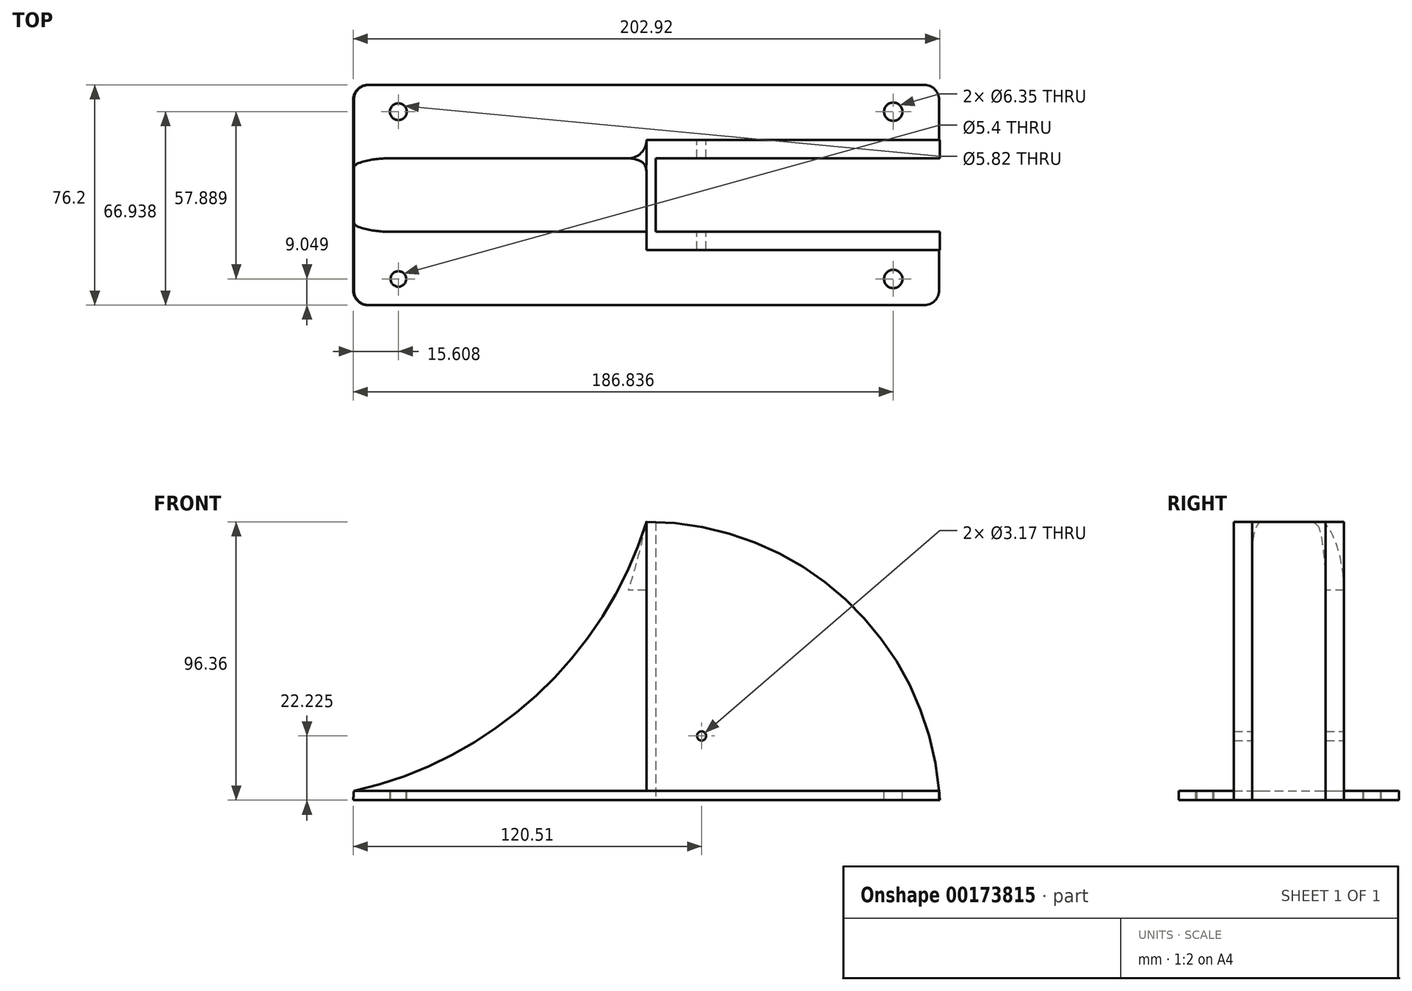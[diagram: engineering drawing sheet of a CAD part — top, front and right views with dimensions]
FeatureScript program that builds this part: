
annotation { "Feature Type Name" : "Feature", "Feature Type Description" : "" }
export const myFeature = defineFeature(function(context is Context, id is Id, definition is map)
    precondition{}
    {
        {
            var Q0;
            Q0=qCreatedBy(makeId("Front.planeOp"),FACE);
            var sketch = newSketch(context, id + "F0", { "sketchPlane" : qUnion([Q0])});
            skLineSegment(sketch, "E0", {"start": v(-101.6, 0) * mm, "end": v(101.6, 0) * mm});
            skArc(sketch, "E1", {"start": v(101.46, 0) * mm, "mid": v(69.96, 68.43) * mm, "end": v(0, 96.36) * mm});
            skLineSegment(sketch, "E2.bottom", {"start": v(-101.6, 0) * mm, "end": v(101.25, 0) * mm});
            skLineSegment(sketch, "E2.top", {"start": v(-101.6, 3.18) * mm, "end": v(101.25, 3.18) * mm});
            skLineSegment(sketch, "E2.left", {"start": v(-101.6, 0) * mm, "end": v(-101.6, 3.18) * mm});
            skLineSegment(sketch, "E2.right", {"start": v(101.25, 0) * mm, "end": v(101.25, 3.18) * mm});
            skLineSegment(sketch, "E3", {"start": v(0, 96.36) * mm, "end": v(0, 3.18) * mm});
            skArc(sketch, "E4", {"start": v(-101.25, 3.18) * mm, "mid": v(-38.14, 36.2) * mm, "end": v(0, 96.36) * mm});
            skArc(sketch, "E5", {"start": v(-101.25, 3.18) * mm, "mid": v(-101.37, 1.59) * mm, "end": v(-101.46, 0) * mm});
            skCircle(sketch, "E6", {"center": v(19.05, 22.23) * mm, "radius": 1.59 * mm});
            skSolve(sketch);
        }
        {
            var Q0;
            {var subQ5=sQuery(id+"F0.wireOp",EDGE,"E2.right");Q0=makeQuery(id+"F0.imprint","IMPRINT",FACE,{"disambiguationData":[TD([[makeQuery(id+"F0.imprint","IMPRINT",EDGE,{"derivedFrom":subQ5}),1.0]])]});}
            extrude(context, id + "F1", {"entities" : qUnion([Q0]), "endBound" : BoundingType.SYMMETRIC, "depth" : 76.2 * mm});
        }
        {
            var Q0;
            {var subQ0=sQuery(id+"F0.wireOp",EDGE,"E2.top");var subQ1=sQuery(id+"F0.wireOp",EDGE,"E1");var subQ3=makeQuery(id+"F0.imprint","INTERSECT",VERTEX,{"derivedFrom":[subQ1,subQ0]});Q0=makeQuery(id+"F0.imprint","IMPRINT",FACE,{"disambiguationData":[TD([[makeQuery(id+"F0.imprint","IMPRINT",EDGE,{"disambiguationData":[TD([[subQ3,1.0]])],"derivedFrom":subQ1}),1.0]])]});}
            extrude(context, id + "F2", {"entities" : qUnion([Q0]), "operationType" : NewBodyOperationType.ADD, "endBound" : BoundingType.SYMMETRIC, "depth" : 38.1 * mm});
        }
        {
            var Q0;
            {var subQ0=sQuery(id+"F0.wireOp",EDGE,"E3");Q0=makeQuery(id+"F0.imprint","IMPRINT",FACE,{"disambiguationData":[TD([[makeQuery(id+"F0.imprint","IMPRINT",EDGE,{"derivedFrom":subQ0}),1.0]])]});}
            extrude(context, id + "F3", {"entities" : qUnion([Q0]), "operationType" : NewBodyOperationType.ADD, "endBound" : BoundingType.SYMMETRIC, "depth" : 38.1 * mm});
        }
        {
            var Q0;
            {var subQ0=sQuery(id+"F0.wireOp",EDGE,"E3");Q0=makeQuery(id+"F0.imprint","IMPRINT",FACE,{"disambiguationData":[TD([[makeQuery(id+"F0.imprint","IMPRINT",EDGE,{"derivedFrom":subQ0}),-1.0]])]});}
            extrude(context, id + "F4", {"entities" : qUnion([Q0]), "operationType" : NewBodyOperationType.ADD, "endBound" : BoundingType.SYMMETRIC, "depth" : 25.4 * mm});
        }
        {
            var Q0;
            Q0=qCreatedBy(makeId("Top.planeOp"),FACE);
            var sketch = newSketch(context, id + "F5", { "sketchPlane" : qUnion([Q0])});
            skLineSegment(sketch, "E7.bottom", {"start": v(130.17, 12.7) * mm, "end": v(3.18, 12.7) * mm});
            skLineSegment(sketch, "E7.top", {"start": v(130.17, -12.7) * mm, "end": v(3.18, -12.7) * mm});
            skLineSegment(sketch, "E7.left", {"start": v(130.17, -12.7) * mm, "end": v(130.17, 12.7) * mm});
            skLineSegment(sketch, "E7.right", {"start": v(3.18, -12.7) * mm, "end": v(3.18, 12.7) * mm});
            skPoint(sketch, "E7.middle", {"position": v(66.67, 0) * mm});
            skPoint(sketch, "E8", {"position": v(3.17, 0) * mm});
            skSolve(sketch);
        }
        {
            var Q0;
            Q0=makeQuery(id+"F5.imprint","IMPRINT",FACE,{"disambiguationData":[TD([[makeQuery(id+"F5.imprint","IMPRINT",EDGE,{"derivedFrom":sQuery(id+"F5.wireOp",EDGE,"E7.bottom")}),1.0]])]});
            extrude(context, id + "F6", {"entities" : qUnion([Q0]), "operationType" : NewBodyOperationType.REMOVE, "endBound" : BoundingType.THROUGH_ALL, "depth" : 127 * mm});
        }
        {
            var Q0;
            Q0=makeQuery(id+"F4.opExtrude","CAP_EDGE",EDGE,{"disambiguationData":[OSD([sQuery(id+"F0.wireOp",EDGE,"E4")])],"isStart":true});
            var Q1;
            Q1=makeQuery(id+"F4.opExtrude","CAP_EDGE",EDGE,{"disambiguationData":[OSD([sQuery(id+"F0.wireOp",EDGE,"E4")])],"isStart":false});
            fillet(context, id + "F7", {"entities" : qUnion([Q0, Q1]), "radius" : 3.17 * mm, "tangentPropagation" : true, "allowEdgeOverflow" : false});
        }
        {
            var Q0;
            Q0=makeQuery(id+"F4.opExtrude","CAP_EDGE",EDGE,{"disambiguationData":[OSD([sQuery(id+"F0.wireOp",EDGE,"E3")])],"isStart":true});
            var Q1;
            Q1=makeQuery(id+"F4.opExtrude","CAP_EDGE",EDGE,{"disambiguationData":[OSD([sQuery(id+"F0.wireOp",EDGE,"E3")])],"isStart":false});
            fillet(context, id + "F8", {"entities" : qUnion([Q0, Q1]), "radius" : 6.35 * mm, "tangentPropagation" : true, "allowEdgeOverflow" : false});
        }
        {
            var Q0;
            Q0=makeQuery(id+"F1.opExtrude","CAP_EDGE",EDGE,{"disambiguationData":[OSD([sQuery(id+"F0.wireOp",EDGE,"E5")])],"isStart":true});
            var Q1;
            Q1=makeQuery(id+"F1.opExtrude","CAP_EDGE",EDGE,{"disambiguationData":[OSD([sQuery(id+"F0.wireOp",EDGE,"E5")])],"isStart":false});
            var Q2;
            Q2=makeQuery(id+"F1.opExtrude","CAP_EDGE",EDGE,{"disambiguationData":[OSD([sQuery(id+"F0.wireOp",EDGE,"E2.right")])],"isStart":true});
            var Q3;
            Q3=makeQuery(id+"F1.opExtrude","CAP_EDGE",EDGE,{"disambiguationData":[OSD([sQuery(id+"F0.wireOp",EDGE,"E2.right")])],"isStart":false});
            fillet(context, id + "F9", {"entities" : qUnion([Q0, Q1, Q2, Q3]), "radius" : 5.08 * mm, "tangentPropagation" : true, "allowEdgeOverflow" : false});
        }
        {
            var Q0;
            {var subQ0=sQuery(id+"F0.wireOp",EDGE,"E2.right");var subQ1=sQuery(id+"F0.wireOp",EDGE,"E1");var subQ4=sQuery(id+"F0.wireOp",EDGE,"E2.top");Q0=makeQuery(id+"F4.boolean.opBoolean","SPLIT",FACE,{"disambiguationData":[TD([makeQuery(id+"F2.opExtrude","CAP_FACE",FACE,{"disambiguationData":[OSD([sQuery(id+"F0.wireOp",EDGE,"E0"),subQ1,subQ0])],"isStart":true})])],"derivedFrom":makeQuery(id+"F1.opExtrude","SWEPT_FACE",FACE,{"disambiguationData":[OSD([subQ4])]})});}
            var sketch = newSketch(context, id + "F10", { "sketchPlane" : qUnion([Q0])});
            skCircle(sketch, "E9", {"center": v(-85.85, 28.84) * mm, "radius": 2.91 * mm});
            skCircle(sketch, "E10", {"center": v(85.38, 28.84) * mm, "radius": 3.18 * mm});
            skCircle(sketch, "E11", {"center": v(-85.85, -29.05) * mm, "radius": 2.7 * mm});
            skCircle(sketch, "E12", {"center": v(85.38, -29.05) * mm, "radius": 3.18 * mm});
            skSolve(sketch);
        }
        {
            var Q0;
            Q0 = qSketchRegion(id + "F10", true);
            extrude(context, id + "F11", {"entities" : qUnion([Q0]), "operationType" : NewBodyOperationType.REMOVE, "endBound" : BoundingType.THROUGH_ALL, "oppositeDirection" : true, "depth" : 25.4 * mm});
        }
    });
